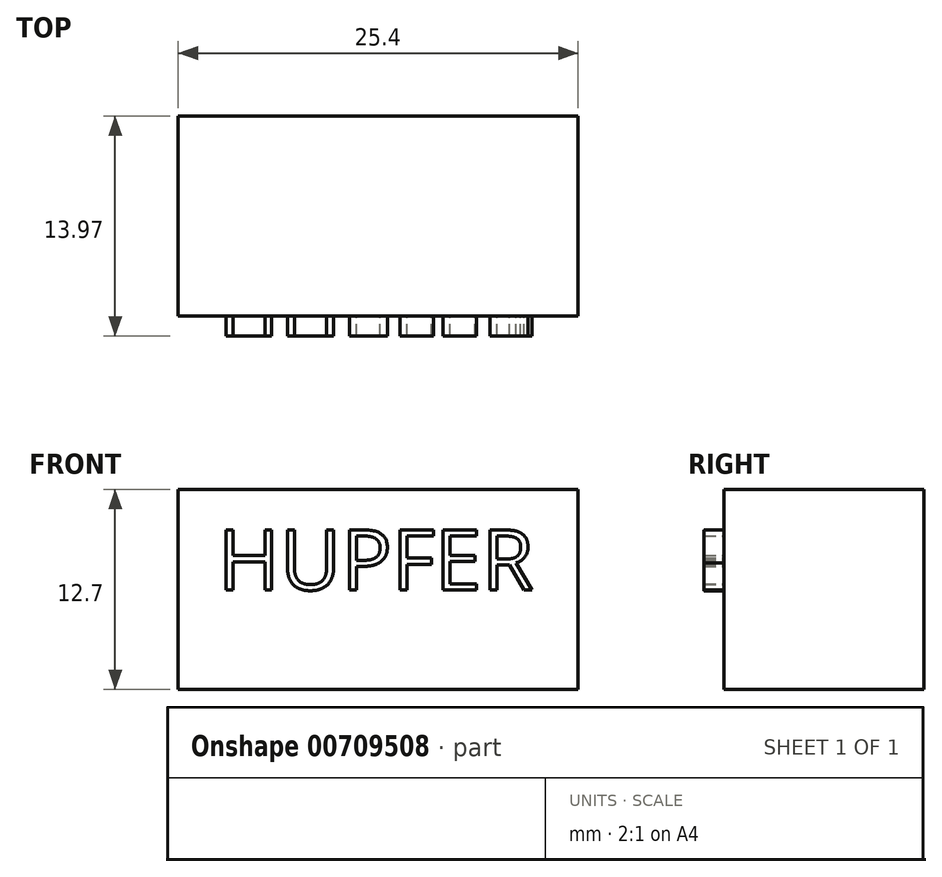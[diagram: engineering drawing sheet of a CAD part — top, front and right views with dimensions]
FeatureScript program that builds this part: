
annotation { "Feature Type Name" : "Feature", "Feature Type Description" : "" }
export const myFeature = defineFeature(function(context is Context, id is Id, definition is map)
    precondition{}
    {
        {
            var Q0;
            Q0=qCreatedBy(makeId("Front.planeOp"),FACE);
            var sketch = newSketch(context, id + "F0", { "sketchPlane" : qUnion([Q0])});
            skLineSegment(sketch, "E0.bottom", {"start": v(-8.93, 9.33) * mm, "end": v(16.47, 9.33) * mm});
            skLineSegment(sketch, "E0.top", {"start": v(-8.93, -3.37) * mm, "end": v(16.47, -3.37) * mm});
            skLineSegment(sketch, "E0.left", {"start": v(-8.93, 9.33) * mm, "end": v(-8.93, -3.37) * mm});
            skLineSegment(sketch, "E0.right", {"start": v(16.47, 9.33) * mm, "end": v(16.47, -3.37) * mm});
            skSolve(sketch);
        }
        {
            var Q0;
            Q0 = qSketchRegion(id + "F0", true);
            extrude(context, id + "F1", {"entities" : qUnion([Q0]), "depth" : 12.7 * mm, "offsetDistance" : 25.4 * mm});
        }
        {
            var Q0;
            Q0=makeQuery(id+"F1.opExtrude","CAP_FACE",FACE,{"disambiguationData":[OSD([sQuery(id+"F0.wireOp",EDGE,"E0.bottom"),sQuery(id+"F0.wireOp",EDGE,"E0.top"),sQuery(id+"F0.wireOp",EDGE,"E0.left"),sQuery(id+"F0.wireOp",EDGE,"E0.right")])],"isStart":false});
            var sketch = newSketch(context, id + "F2", { "sketchPlane" : qUnion([Q0])});
            skText(sketch, "E1", { "text": "HUPFER", "fontName": "OpenSans-Regular.ttf"});
            const initialGuessF2  = {"E1": [-0.0064, 0.00295, 1, 0, 0.00384]};
            skSetInitialGuess(sketch, initialGuessF2);
            skSolve(sketch);
        }
        {
            var Q0;
            Q0 = qSketchRegion(id + "F2", true);
            extrude(context, id + "F3", {"entities" : qUnion([Q0]), "operationType" : NewBodyOperationType.ADD, "depth" : 1.27 * mm, "offsetDistance" : 25.4 * mm});
        }
    });
